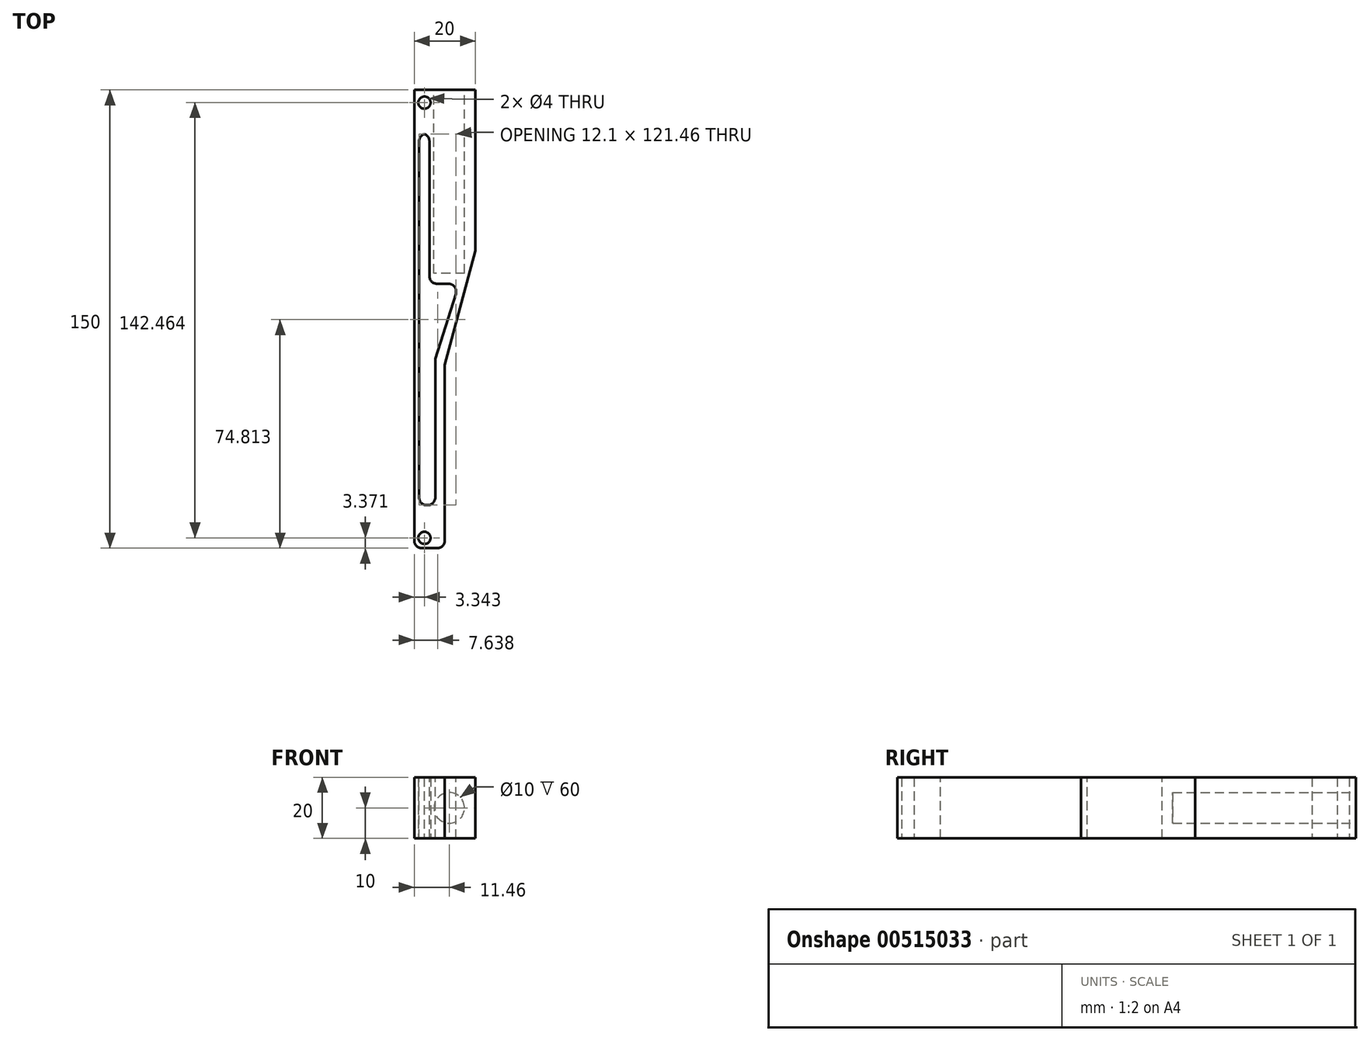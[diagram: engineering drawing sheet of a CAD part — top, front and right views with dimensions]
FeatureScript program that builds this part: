
annotation { "Feature Type Name" : "Feature", "Feature Type Description" : "" }
export const myFeature = defineFeature(function(context is Context, id is Id, definition is map)
    precondition{}
    {
        {
            var Q0;
            Q0=qCreatedBy(makeId("Top.planeOp"),FACE);
            var sketch = newSketch(context, id + "F0", { "sketchPlane" : qUnion([Q0])});
            skLineSegment(sketch, "E0.bottom", {"start": v(-71.04, 71.64) * mm, "end": v(-51.04, 71.64) * mm});
            skLineSegment(sketch, "E0.top", {"start": v(-71.04, -78.36) * mm, "end": v(-51.04, -78.36) * mm});
            skLineSegment(sketch, "E0.left", {"start": v(-71.04, 71.64) * mm, "end": v(-71.04, -78.36) * mm});
            skLineSegment(sketch, "E0.right", {"start": v(-51.04, 71.64) * mm, "end": v(-51.04, -78.36) * mm});
            skSolve(sketch);
        }
        {
            var Q0;
            Q0=makeQuery(id+"F0.imprint","IMPRINT",FACE,{"disambiguationData":[TD([[makeQuery(id+"F0.imprint","IMPRINT",EDGE,{"derivedFrom":sQuery(id+"F0.wireOp",EDGE,"E0.bottom")}),-1.0]])]});
            extrude(context, id + "F1", {"entities" : qUnion([Q0]), "depth" : 10 * mm, "offsetDistance" : 25 * mm});
        }
        {
            var Q0;
            Q0=makeQuery(id+"FomEpZF3jwlUIwq_1.opExtrude","SWEPT_EDGE",EDGE,{"disambiguationData":[OSD([sQuery(id+"F0.wireOp",EDGE,"E0.left"),sQuery(id+"F1NLpkMIvdNk7jU_1.wireOp",EDGE,"JdDga99X-qCnD-vict-qKIc-81UAap1c88fU.top"),sQuery(id+"F1NLpkMIvdNk7jU_1.wireOp",EDGE,"JdDga99X-qCnD-vict-qKIc-81UAap1c88fU.right")])]});
            var Q1;
            Q1=makeQuery(id+"FomEpZF3jwlUIwq_1.opExtrude","CAP_EDGE",EDGE,{"disambiguationData":[OSD([sQuery(id+"F1NLpkMIvdNk7jU_1.wireOp",EDGE,"JdDga99X-qCnD-vict-qKIc-81UAap1c88fU.top")])],"isStart":false});
            var Q2;
            Q2=makeQuery(id+"F5s1CBushxTlWOC_1.boolean.opBoolean","MERGE",EDGE,{"derivedFrom":[makeQuery(id+"FomEpZF3jwlUIwq_1.boolean.opBoolean","MERGE",EDGE,{"derivedFrom":[makeQuery(id+"F1.opExtrude","CAP_EDGE",EDGE,{"disambiguationData":[OSD([sQuery(id+"F0.wireOp",EDGE,"E0.top")])],"isStart":false}),makeQuery(id+"FomEpZF3jwlUIwq_1.opExtrude","SWEPT_EDGE",EDGE,{"disambiguationData":[OSD([sQuery(id+"F1NLpkMIvdNk7jU_1.wireOp",EDGE,"JdDga99X-qCnD-vict-qKIc-81UAap1c88fU.top"),sQuery(id+"F1NLpkMIvdNk7jU_1.wireOp",EDGE,"JdDga99X-qCnD-vict-qKIc-81UAap1c88fU.left")])]})]}),makeQuery(id+"F5s1CBushxTlWOC_1.opExtrude","SWEPT_EDGE",EDGE,{"disambiguationData":[OSD([sQuery(id+"FOXx8H1SDtEovMQ_1.wireOp",EDGE,"FEWDH13M-Medy-eiIw-sagk-Jp41e8USBhHK.top"),sQuery(id+"FOXx8H1SDtEovMQ_1.wireOp",EDGE,"FEWDH13M-Medy-eiIw-sagk-Jp41e8USBhHK.left")])]})]});
            var Q3;
            Q3=makeQuery(id+"F5s1CBushxTlWOC_1.opExtrude","SWEPT_EDGE",EDGE,{"disambiguationData":[OSD([sQuery(id+"F0.wireOp",EDGE,"E0.right"),sQuery(id+"FOXx8H1SDtEovMQ_1.wireOp",EDGE,"FEWDH13M-Medy-eiIw-sagk-Jp41e8USBhHK.top"),sQuery(id+"FOXx8H1SDtEovMQ_1.wireOp",EDGE,"FEWDH13M-Medy-eiIw-sagk-Jp41e8USBhHK.right")])]});
            var Q4;
            Q4=makeQuery(id+"F5s1CBushxTlWOC_1.opExtrude","CAP_EDGE",EDGE,{"disambiguationData":[OSD([sQuery(id+"FOXx8H1SDtEovMQ_1.wireOp",EDGE,"FEWDH13M-Medy-eiIw-sagk-Jp41e8USBhHK.top")])],"isStart":false});
            var Q5;
            Q5=makeQuery(id+"F5s1CBushxTlWOC_1.opExtrude","CAP_EDGE",EDGE,{"disambiguationData":[OSD([sQuery(id+"FOXx8H1SDtEovMQ_1.wireOp",EDGE,"FEWDH13M-Medy-eiIw-sagk-Jp41e8USBhHK.left")])],"isStart":false});
            var Q6;
            Q6=makeQuery(id+"FomEpZF3jwlUIwq_1.opExtrude","CAP_EDGE",EDGE,{"disambiguationData":[OSD([sQuery(id+"F1NLpkMIvdNk7jU_1.wireOp",EDGE,"JdDga99X-qCnD-vict-qKIc-81UAap1c88fU.left")])],"isStart":false});
            var Q7;
            Q7=makeQuery(id+"FomEpZF3jwlUIwq_1.opExtrude","CAP_EDGE",EDGE,{"disambiguationData":[OSD([sQuery(id+"F1NLpkMIvdNk7jU_1.wireOp",EDGE,"JdDga99X-qCnD-vict-qKIc-81UAap1c88fU.right")])],"isStart":false});
            var Q8;
            Q8=makeQuery(id+"F5s1CBushxTlWOC_1.opExtrude","CAP_EDGE",EDGE,{"disambiguationData":[OSD([sQuery(id+"FOXx8H1SDtEovMQ_1.wireOp",EDGE,"FEWDH13M-Medy-eiIw-sagk-Jp41e8USBhHK.right")])],"isStart":false});
            var Q9;
            Q9=makeQuery(id+"F5s1CBushxTlWOC_1.opExtrude","CAP_EDGE",EDGE,{"disambiguationData":[OSD([sQuery(id+"FOXx8H1SDtEovMQ_1.wireOp",EDGE,"FEWDH13M-Medy-eiIw-sagk-Jp41e8USBhHK.bottom")])],"isStart":false});
            var Q10;
            Q10=makeQuery(id+"F5s1CBushxTlWOC_1.boolean.opBoolean","MERGE",EDGE,{"derivedFrom":[makeQuery(id+"FomEpZF3jwlUIwq_1.boolean.opBoolean","MERGE",EDGE,{"derivedFrom":[makeQuery(id+"F1.opExtrude","CAP_EDGE",EDGE,{"disambiguationData":[OSD([sQuery(id+"F0.wireOp",EDGE,"E0.top")])],"isStart":true}),makeQuery(id+"FomEpZF3jwlUIwq_1.opExtrude","SWEPT_EDGE",EDGE,{"disambiguationData":[OSD([sQuery(id+"F1NLpkMIvdNk7jU_1.wireOp",EDGE,"JdDga99X-qCnD-vict-qKIc-81UAap1c88fU.bottom"),sQuery(id+"F1NLpkMIvdNk7jU_1.wireOp",EDGE,"JdDga99X-qCnD-vict-qKIc-81UAap1c88fU.left")])]})]}),makeQuery(id+"F5s1CBushxTlWOC_1.opExtrude","SWEPT_EDGE",EDGE,{"disambiguationData":[OSD([sQuery(id+"FOXx8H1SDtEovMQ_1.wireOp",EDGE,"FEWDH13M-Medy-eiIw-sagk-Jp41e8USBhHK.bottom"),sQuery(id+"FOXx8H1SDtEovMQ_1.wireOp",EDGE,"FEWDH13M-Medy-eiIw-sagk-Jp41e8USBhHK.left")])]})]});
            var Q11;
            Q11=makeQuery(id+"FomEpZF3jwlUIwq_1.opExtrude","CAP_EDGE",EDGE,{"disambiguationData":[OSD([sQuery(id+"F1NLpkMIvdNk7jU_1.wireOp",EDGE,"JdDga99X-qCnD-vict-qKIc-81UAap1c88fU.bottom")])],"isStart":false});
            var Q12;
            Q12=makeQuery(id+"F5s1CBushxTlWOC_1.opExtrude","SWEPT_EDGE",EDGE,{"disambiguationData":[OSD([sQuery(id+"F0.wireOp",EDGE,"E0.right"),sQuery(id+"FOXx8H1SDtEovMQ_1.wireOp",EDGE,"FEWDH13M-Medy-eiIw-sagk-Jp41e8USBhHK.bottom"),sQuery(id+"FOXx8H1SDtEovMQ_1.wireOp",EDGE,"FEWDH13M-Medy-eiIw-sagk-Jp41e8USBhHK.right")])]});
            var Q13;
            Q13=makeQuery(id+"FomEpZF3jwlUIwq_1.opExtrude","SWEPT_EDGE",EDGE,{"disambiguationData":[OSD([sQuery(id+"F0.wireOp",EDGE,"E0.left"),sQuery(id+"F1NLpkMIvdNk7jU_1.wireOp",EDGE,"JdDga99X-qCnD-vict-qKIc-81UAap1c88fU.bottom"),sQuery(id+"F1NLpkMIvdNk7jU_1.wireOp",EDGE,"JdDga99X-qCnD-vict-qKIc-81UAap1c88fU.right")])]});
            fillet(context, id + "F2", {"entities" : qUnion([Q0, Q1, Q2, Q3, Q4, Q5, Q6, Q7, Q8, Q9, Q10, Q11, Q12, Q13]), "radius" : 2.5 * mm, "tangentPropagation" : true, "allowEdgeOverflow" : false});
        }
        {
            var Q0;
            {var subQ0=sQuery(id+"Fe1uJ81IbgYl2Ml_1.wireOp",EDGE,"cKE2W4Qr-xIU3-4X3f-CdDW-XdCW86x1bF6O.right");var subQ1=sQuery(id+"F0.wireOp",EDGE,"E0.right");Q0=makeQuery(id+"FoZkqRhm2qEG9oC_1.boolean.opBoolean","MERGE",FACE,{"derivedFrom":[makeQuery(id+"FjW8aT6Y56iKWgf_1.boolean.opBoolean","MERGE",FACE,{"derivedFrom":[makeQuery(id+"F1.opExtrude","SWEPT_FACE",FACE,{"disambiguationData":[OSD([subQ1])]}),makeQuery(id+"FjW8aT6Y56iKWgf_1.opExtrude","SWEPT_FACE",FACE,{"disambiguationData":[OSD([subQ0])]})]}),makeQuery(id+"FoZkqRhm2qEG9oC_1.opExtrude","SWEPT_FACE",FACE,{"disambiguationData":[OSD([subQ1,sQuery(id+"Fe1uJ81IbgYl2Ml_1.wireOp",EDGE,"cKE2W4Qr-xIU3-4X3f-CdDW-XdCW86x1bF6O.top"),subQ0])]})]});}
            var sketch = newSketch(context, id + "F3", { "sketchPlane" : qUnion([Q0])});
            skCircle(sketch, "E1", {"center": v(-74.99, 3.34) * mm, "radius": 2 * mm});
            skCircle(sketch, "E2", {"center": v(67.48, 3.34) * mm, "radius": 2 * mm});
            skSolve(sketch);
        }
        {
            var Q0;
            Q0=makeQuery(id+"F3.imprint","IMPRINT",FACE,{"disambiguationData":[TD([[makeQuery(id+"F3.imprint","IMPRINT",EDGE,{"derivedFrom":sQuery(id+"F3.wireOp",EDGE,"E1")}),1.0]])]});
            extrude(context, id + "F4", {"entities" : qUnion([Q0]), "operationType" : NewBodyOperationType.REMOVE, "oppositeDirection" : true, "depth" : 60 * mm, "offsetDistance" : 25 * mm});
        }
        {
            var Q0;
            Q0=makeQuery(id+"F1.opExtrude","CAP_FACE",FACE,{"disambiguationData":[OSD([sQuery(id+"F0.wireOp",EDGE,"E0.bottom"),sQuery(id+"F0.wireOp",EDGE,"E0.top"),sQuery(id+"F0.wireOp",EDGE,"E0.left"),sQuery(id+"F0.wireOp",EDGE,"E0.right")])],"isStart":false});
            var sketch = newSketch(context, id + "F5", { "sketchPlane" : qUnion([Q0])});
            skLineSegment(sketch, "E3", {"start": v(-51.04, 71.64) * mm, "end": v(-51.04, -18.36) * mm});
            skLineSegment(sketch, "E4", {"start": v(-51.04, -18.36) * mm, "end": v(-71.04, -18.36) * mm});
            skSolve(sketch);
        }
        {
            var Q0;
            Q0=makeQuery(id+"F5.imprint","IMPRINT",FACE,{"disambiguationData":[TD([[makeQuery(id+"F5.imprint","IMPRINT",EDGE,{"derivedFrom":sQuery(id+"F5.wireOp",EDGE,"E3")}),-1.0]])]});
            extrude(context, id + "F6", {"entities" : qUnion([Q0]), "operationType" : NewBodyOperationType.ADD, "depth" : 10 * mm, "offsetDistance" : 25 * mm});
        }
        {
            var Q0;
            Q0=makeQuery(id+"F6.opExtrude","CAP_EDGE",EDGE,{"disambiguationData":[OSD([sQuery(id+"F5.wireOp",EDGE,"E4")])],"isStart":false});
            chamfer(context, id + "F7", {"entities" : qUnion([Q0]), "chamferType" : ChamferType.OFFSET_ANGLE, "width" : 10 * mm, "oppositeDirection" : false, "angle" : 75 * degree, "tangentPropagation" : true});
        }
        {
            var Q0;
            {var subQ0=sQuery(id+"F0.wireOp",EDGE,"E0.bottom");Q0=makeQuery(id+"F6.boolean.opBoolean","MERGE",FACE,{"derivedFrom":[makeQuery(id+"F1.opExtrude","SWEPT_FACE",FACE,{"disambiguationData":[OSD([subQ0])]}),makeQuery(id+"F6.opExtrude","SWEPT_FACE",FACE,{"disambiguationData":[OSD([subQ0])]})]});}
            var sketch = newSketch(context, id + "F8", { "sketchPlane" : qUnion([Q0])});
            skCircle(sketch, "E5", {"center": v(61.04, 11.46) * mm, "radius": 5 * mm});
            skPoint(sketch, "E5.centerSnap0", {"position": v(61.04, 20) * mm});
            skSolve(sketch);
        }
        {
            var Q0;
            Q0=makeQuery(id+"F8.imprint","IMPRINT",FACE,{"disambiguationData":[TD([[makeQuery(id+"F8.imprint","IMPRINT",EDGE,{"derivedFrom":sQuery(id+"F8.wireOp",EDGE,"E5")}),1.0]])]});
            extrude(context, id + "F9", {"entities" : qUnion([Q0]), "operationType" : NewBodyOperationType.REMOVE, "oppositeDirection" : true, "depth" : 60 * mm, "offsetDistance" : 25 * mm});
        }
        {
            var Q0;
            Q0=makeQuery(id+"F3.imprint","IMPRINT",FACE,{"disambiguationData":[TD([[makeQuery(id+"F3.imprint","IMPRINT",EDGE,{"derivedFrom":sQuery(id+"F3.wireOp",EDGE,"E2")}),1.0]])]});
            extrude(context, id + "F10", {"entities" : qUnion([Q0]), "operationType" : NewBodyOperationType.REMOVE, "oppositeDirection" : true, "depth" : 50 * mm, "offsetDistance" : 25 * mm});
        }
        {
            var Q0;
            {var subQ0=sQuery(id+"F0.wireOp",EDGE,"E0.left");Q0=makeQuery(id+"F6.boolean.opBoolean","MERGE",FACE,{"derivedFrom":[makeQuery(id+"F1.opExtrude","SWEPT_FACE",FACE,{"disambiguationData":[OSD([subQ0])]}),makeQuery(id+"F6.opExtrude","SWEPT_FACE",FACE,{"disambiguationData":[OSD([subQ0])]})]});}
            var sketch = newSketch(context, id + "F11", { "sketchPlane" : qUnion([Q0])});
            skLineSegment(sketch, "E6", {"start": v(-8.18, 14.6) * mm, "end": v(-8.18, 6.87) * mm});
            skLineSegment(sketch, "E7", {"start": v(-8.18, 6.87) * mm, "end": v(16.33, 6.87) * mm});
            skLineSegment(sketch, "E8", {"start": v(16.33, 6.87) * mm, "end": v(-8.18, 14.6) * mm});
            skLineSegment(sketch, "E9", {"start": v(-57.32, 4.96) * mm, "end": v(-57.32, 1.59) * mm});
            skLineSegment(sketch, "E10", {"start": v(-57.32, 1.59) * mm, "end": v(64.28, 1.59) * mm});
            skLineSegment(sketch, "E11", {"start": v(64.28, 1.59) * mm, "end": v(64.28, 6.87) * mm});
            skLineSegment(sketch, "E12", {"start": v(64.28, 6.87) * mm, "end": v(16.33, 6.87) * mm});
            skLineSegment(sketch, "E13", {"start": v(-57.32, 4.96) * mm, "end": v(-8.18, 4.96) * mm});
            skLineSegment(sketch, "E14", {"start": v(-8.18, 4.96) * mm, "end": v(-8.18, 6.87) * mm});
            skSolve(sketch);
        }
        {
            var Q0;
            Q0=makeQuery(id+"F11.imprint","IMPRINT",FACE,{"disambiguationData":[TD([[makeQuery(id+"F11.imprint","IMPRINT",EDGE,{"derivedFrom":sQuery(id+"F11.wireOp",EDGE,"E7")}),-1.0]])]});
            var Q1;
            Q1=makeQuery(id+"F11.imprint","IMPRINT",FACE,{"disambiguationData":[TD([[makeQuery(id+"F11.imprint","IMPRINT",EDGE,{"derivedFrom":sQuery(id+"F11.wireOp",EDGE,"E6")}),1.0]])]});
            extrude(context, id + "F12", {"entities" : qUnion([Q0, Q1]), "operationType" : NewBodyOperationType.REMOVE, "oppositeDirection" : true, "depth" : 40 * mm, "offsetDistance" : 25 * mm});
        }
        {
            var Q0;
            Q0=makeQuery(id+"F12.boolean.opBoolean","COPY",EDGE,{"derivedFrom":makeQuery(id+"F12.opExtrude","SWEPT_EDGE",EDGE,{"disambiguationData":[OSD([sQuery(id+"F11.wireOp",EDGE,"E6"),sQuery(id+"F11.wireOp",EDGE,"E8")])]})});
            var Q1;
            Q1=makeQuery(id+"F12.boolean.opBoolean","COPY",EDGE,{"derivedFrom":makeQuery(id+"F12.opExtrude","SWEPT_EDGE",EDGE,{"disambiguationData":[OSD([sQuery(id+"F11.wireOp",EDGE,"E13"),sQuery(id+"F11.wireOp",EDGE,"E14")])]})});
            var Q2;
            Q2=makeQuery(id+"F12.boolean.opBoolean","COPY",EDGE,{"derivedFrom":makeQuery(id+"F12.opExtrude","SWEPT_EDGE",EDGE,{"disambiguationData":[OSD([sQuery(id+"F11.wireOp",EDGE,"E11"),sQuery(id+"F11.wireOp",EDGE,"E12")])]})});
            var Q3;
            Q3=makeQuery(id+"F12.boolean.opBoolean","COPY",EDGE,{"derivedFrom":makeQuery(id+"F12.opExtrude","SWEPT_EDGE",EDGE,{"disambiguationData":[OSD([sQuery(id+"F11.wireOp",EDGE,"E10"),sQuery(id+"F11.wireOp",EDGE,"E11")])]})});
            var Q4;
            Q4=makeQuery(id+"F12.boolean.opBoolean","COPY",EDGE,{"derivedFrom":makeQuery(id+"F12.opExtrude","SWEPT_EDGE",EDGE,{"disambiguationData":[OSD([sQuery(id+"F11.wireOp",EDGE,"E9"),sQuery(id+"F11.wireOp",EDGE,"E10")])]})});
            var Q5;
            Q5=makeQuery(id+"F12.boolean.opBoolean","COPY",EDGE,{"derivedFrom":makeQuery(id+"F12.opExtrude","SWEPT_EDGE",EDGE,{"disambiguationData":[OSD([sQuery(id+"F11.wireOp",EDGE,"E9"),sQuery(id+"F11.wireOp",EDGE,"E13")])]})});
            fillet(context, id + "F13", {"entities" : qUnion([Q0, Q1, Q2, Q3, Q4, Q5]), "radius" : 2.5 * mm, "tangentPropagation" : true, "allowEdgeOverflow" : false});
        }
        {
            var Q0;
            Q0=makeQuery(id+"F1.opExtrude","SWEPT_BODY",BODY,{"disambiguationData":[OSD([sQuery(id+"F0.wireOp",EDGE,"E0.bottom"),sQuery(id+"F0.wireOp",EDGE,"E0.top"),sQuery(id+"F0.wireOp",EDGE,"E0.left"),sQuery(id+"F0.wireOp",EDGE,"E0.right")])]});
            var Q1;
            Q1=makeQuery(id+"F6.opExtrude","CAP_EDGE",EDGE,{"disambiguationData":[OSD([sQuery(id+"F5.wireOp",EDGE,"E3")])],"isStart":false});
            transform(context, id + "F14", {"entities" : qUnion([Q0]), "transformType" : TransformType.ROTATION, "transformAxis" : qUnion([Q1]), "angle" : 90 * degree, "oppositeDirection" : true, "makeCopy" : false});
        }
    });
